# Revit family: CHI_Overhead_MaxClean_MC250
name_source: partatom
category: Doors
units: mm (PartAtom-declared; Revit-internal decimal feet)

## family parameters
Always vertical = Yes
Cut with Voids When Loaded = No
Host = Wall
OmniClass Number = 23.30.10.00
OmniClass Title = Doors
Room Calculation Point = No
Shared = No

## types (1)
- CHI_Overhead_MaxClean_MC250
    Analytic Construction = <None>
    Control Panel Height = 3' - 0 3/16"
    Curtain Material = PVC Blue
    Description = High Performance Vinyl Doors
    Expected Lifespan (Years) = 0
    Frame Projection Ext. = 0' - 1"
    Frame Projection Int. = 0' - 1"
    Frame Width = 0' - 3"
    Function = Interior
    Height = 8' - 0"
    Hood & Motor Cover Material = 304 Stainless Steel Slanted
    Maintenance Schedule (Months) = 0
    Manufacturer = PerforMax Global
    Max Height = 0' - 0"
    Max Width = 0' - 0"
    Model = MaxClean - MC250
    RO Offset = 0' - 0"
    Thickness = 0' - 0"
    URL = https://performaxglobal.com
    Vision Panel Material = Anti-UV
    Voltage_MEP = 0 V
    Wall Closure = By host
    Warranty Duration (Years) = 0
    Width = 8' - 0"

## geometry (parser evidence)
native form markers: Sweep x7
no freeform markers — native parametric forms only
